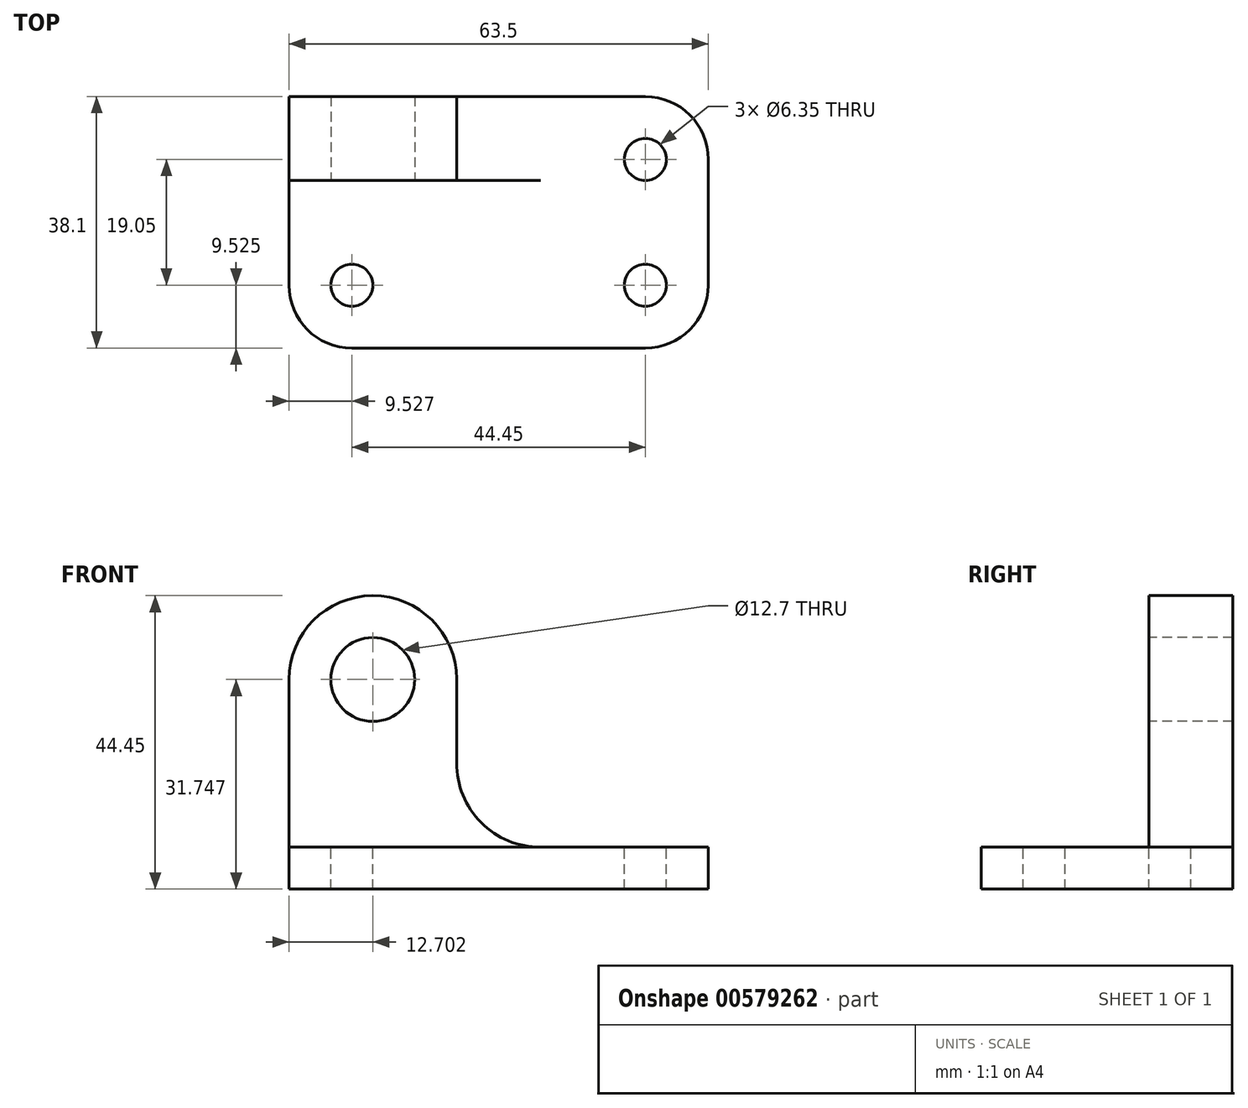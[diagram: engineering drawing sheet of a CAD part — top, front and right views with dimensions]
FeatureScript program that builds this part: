
annotation { "Feature Type Name" : "Feature", "Feature Type Description" : "" }
export const myFeature = defineFeature(function(context is Context, id is Id, definition is map)
    precondition{}
    {
        {
            var Q0;
            Q0=qCreatedBy(makeId("Front.planeOp"),FACE);
            var sketch = newSketch(context, id + "F0", { "sketchPlane" : qUnion([Q0])});
            skLineSegment(sketch, "E0", {"start": v(-165.52, 134.05) * mm, "end": v(-165.52, 89.6) * mm});
            skLineSegment(sketch, "E1", {"start": v(-165.52, 89.6) * mm, "end": v(-102.02, 89.6) * mm});
            skLineSegment(sketch, "E2", {"start": v(-102.02, 89.6) * mm, "end": v(-102.02, 95.95) * mm});
            skLineSegment(sketch, "E3", {"start": v(-102.02, 95.95) * mm, "end": v(-127.42, 95.95) * mm});
            skLineSegment(sketch, "E4", {"start": v(-127.42, 95.95) * mm, "end": v(-127.42, 134.05) * mm});
            skLineSegment(sketch, "E5", {"start": v(-127.42, 134.05) * mm, "end": v(-165.52, 134.05) * mm});
            skSolve(sketch);
        }
        {
            var Q0;
            Q0=makeQuery(id+"F0.imprint","IMPRINT",FACE,{"disambiguationData":[TD([[makeQuery(id+"F0.imprint","IMPRINT",EDGE,{"derivedFrom":sQuery(id+"F0.wireOp",EDGE,"E0")}),1.0]])]});
            extrude(context, id + "F1", {"entities" : qUnion([Q0]), "depth" : 38.1 * mm, "offsetDistance" : 25.4 * mm});
        }
        {
            var Q0;
            Q0=makeQuery(id+"F1.opExtrude","SWEPT_FACE",FACE,{"disambiguationData":[OSD([sQuery(id+"F0.wireOp",EDGE,"E4")])]});
            var sketch = newSketch(context, id + "F2", { "sketchPlane" : qUnion([Q0])});
            skLineSegment(sketch, "E6", {"start": v(-12.7, 134.05) * mm, "end": v(-12.7, 95.95) * mm});
            skSolve(sketch);
        }
        {
            var Q0;
            {var subQ0=sQuery(id+"F2.wireOp",EDGE,"E6");Q0=makeQuery(id+"F2.imprint","IMPRINT",FACE,{"disambiguationData":[TD([[makeQuery(id+"F2.imprint","IMPRINT",EDGE,{"derivedFrom":subQ0}),-1.0]])]});}
            extrude(context, id + "F3", {"entities" : qUnion([Q0]), "operationType" : NewBodyOperationType.REMOVE, "endBound" : BoundingType.THROUGH_ALL, "oppositeDirection" : true, "depth" : 25.4 * mm, "offsetDistance" : 25.4 * mm});
        }
        {
            var Q0;
            Q0=makeQuery(id+"F3.boolean.opBoolean","COPY",FACE,{"derivedFrom":makeQuery(id+"F3.opExtrude","SWEPT_FACE",FACE,{"disambiguationData":[OSD([sQuery(id+"F2.wireOp",EDGE,"E6")])]})});
            var sketch = newSketch(context, id + "F4", { "sketchPlane" : qUnion([Q0])});
            skCircle(sketch, "E7", {"center": v(-152.82, 121.35) * mm, "radius": 6.35 * mm});
            skCircle(sketch, "E8", {"center": v(-152.82, 121.35) * mm, "radius": 12.7 * mm});
            skSolve(sketch);
        }
        {
            var Q0;
            Q0=makeQuery(id+"F4.imprint","IMPRINT",FACE,{"disambiguationData":[TD([[makeQuery(id+"F4.imprint","IMPRINT",EDGE,{"derivedFrom":sQuery(id+"F4.wireOp",EDGE,"E7")}),1.0]])]});
            var Q1;
            {var subQ0=sQuery(id+"F4.wireOp",EDGE,"E8");var subQ1=sQuery(id+"F2.wireOp",EDGE,"E6");var subQ4=makeQuery(id+"F3.boolean.opBoolean","INTERSECT",EDGE,{"derivedFrom":[makeQuery(id+"F1.opExtrude","SWEPT_FACE",FACE,{"disambiguationData":[OSD([sQuery(id+"F0.wireOp",EDGE,"E0")])]}),makeQuery(id+"F3.opExtrude","SWEPT_FACE",FACE,{"disambiguationData":[OSD([subQ1])]})]});var subQ5=makeQuery(id+"F4.imprint","INTERSECT",VERTEX,{"derivedFrom":[subQ4,subQ0]});Q1=makeQuery(id+"F4.imprint","IMPRINT",FACE,{"disambiguationData":[TD([[makeQuery(id+"F4.imprint","IMPRINT",EDGE,{"disambiguationData":[TD([[subQ5,1.0]])],"derivedFrom":subQ0}),-1.0]])]});}
            extrude(context, id + "F5", {"entities" : qUnion([Q0, Q1]), "operationType" : NewBodyOperationType.REMOVE, "endBound" : BoundingType.THROUGH_ALL, "oppositeDirection" : true, "depth" : 25.4 * mm, "offsetDistance" : 25.4 * mm});
        }
        {
            var Q0;
            Q0=makeQuery(id+"F3.boolean.opBoolean","COPY",FACE,{"derivedFrom":makeQuery(id+"F3.opExtrude","SWEPT_FACE",FACE,{"disambiguationData":[OSD([sQuery(id+"F2.wireOp",EDGE,"E6")])]})});
            var sketch = newSketch(context, id + "F6", { "sketchPlane" : qUnion([Q0])});
            skArc(sketch, "E9", {"start": v(-140.12, 121.42) * mm, "mid": v(-143.86, 130.35) * mm, "end": v(-152.82, 134.05) * mm});
            skArc(sketch, "E10", {"start": v(-140.12, 108.72) * mm, "mid": v(-136.42, 99.7) * mm, "end": v(-127.42, 95.95) * mm});
            skPoint(sketch, "E10.startSnap0", {"position": v(-140.12, 134.05) * mm});
            skLineSegment(sketch, "E11", {"start": v(-140.12, 121.42) * mm, "end": v(-140.12, 108.72) * mm});
            skSolve(sketch);
        }
        {
            var Q0;
            Q0=makeQuery(id+"F6.imprint","IMPRINT",FACE,{"disambiguationData":[TD([[makeQuery(id+"F6.imprint","IMPRINT",EDGE,{"derivedFrom":sQuery(id+"F6.wireOp",EDGE,"E9")}),-1.0]])]});
            extrude(context, id + "F7", {"entities" : qUnion([Q0]), "operationType" : NewBodyOperationType.REMOVE, "endBound" : BoundingType.THROUGH_ALL, "oppositeDirection" : true, "depth" : 25.4 * mm, "offsetDistance" : 25.4 * mm});
        }
        {
            var Q0;
            {var subQ0=sQuery(id+"F0.wireOp",EDGE,"E3");Q0=makeQuery(id+"F3.boolean.opBoolean","MERGE",FACE,{"derivedFrom":[makeQuery(id+"F1.opExtrude","SWEPT_FACE",FACE,{"disambiguationData":[OSD([subQ0])]}),makeQuery(id+"F3.opExtrude","SWEPT_FACE",FACE,{"disambiguationData":[OSD([subQ0,sQuery(id+"F0.wireOp",EDGE,"E4")])]})]});}
            var sketch = newSketch(context, id + "F8", { "sketchPlane" : qUnion([Q0])});
            skCircle(sketch, "E12", {"center": v(-156, -28.58) * mm, "radius": 3.18 * mm});
            skCircle(sketch, "E13", {"center": v(-111.54, -28.58) * mm, "radius": 3.18 * mm});
            skCircle(sketch, "E14", {"center": v(-111.54, -9.52) * mm, "radius": 3.17 * mm});
            skSolve(sketch);
        }
        {
            var Q0;
            Q0=makeQuery(id+"F8.imprint","IMPRINT",FACE,{"disambiguationData":[TD([[makeQuery(id+"F8.imprint","IMPRINT",EDGE,{"derivedFrom":sQuery(id+"F8.wireOp",EDGE,"E12")}),1.0]])]});
            var Q1;
            Q1=makeQuery(id+"F8.imprint","IMPRINT",FACE,{"disambiguationData":[TD([[makeQuery(id+"F8.imprint","IMPRINT",EDGE,{"derivedFrom":sQuery(id+"F8.wireOp",EDGE,"E13")}),1.0]])]});
            var Q2;
            Q2=makeQuery(id+"F8.imprint","IMPRINT",FACE,{"disambiguationData":[TD([[makeQuery(id+"F8.imprint","IMPRINT",EDGE,{"derivedFrom":sQuery(id+"F8.wireOp",EDGE,"E14")}),1.0]])]});
            extrude(context, id + "F9", {"entities" : qUnion([Q0, Q1, Q2]), "operationType" : NewBodyOperationType.REMOVE, "endBound" : BoundingType.THROUGH_ALL, "oppositeDirection" : true, "depth" : 25.4 * mm, "offsetDistance" : 25.4 * mm});
        }
        {
            var Q0;
            {var subQ0=sQuery(id+"F0.wireOp",EDGE,"E3");Q0=makeQuery(id+"F3.boolean.opBoolean","MERGE",FACE,{"derivedFrom":[makeQuery(id+"F1.opExtrude","SWEPT_FACE",FACE,{"disambiguationData":[OSD([subQ0])]}),makeQuery(id+"F3.opExtrude","SWEPT_FACE",FACE,{"disambiguationData":[OSD([subQ0,sQuery(id+"F0.wireOp",EDGE,"E4")])]})]});}
            var sketch = newSketch(context, id + "F10", { "sketchPlane" : qUnion([Q0])});
            skCircle(sketch, "E15", {"center": v(-156, -28.58) * mm, "radius": 9.53 * mm});
            skCircle(sketch, "E16", {"center": v(-111.54, -28.58) * mm, "radius": 9.53 * mm});
            skCircle(sketch, "E17", {"center": v(-111.54, -9.52) * mm, "radius": 9.53 * mm});
            skSolve(sketch);
        }
        {
            var Q0;
            {var subQ0=sQuery(id+"F10.wireOp",EDGE,"E15");var subQ1=sQuery(id+"F0.wireOp",EDGE,"E4");var subQ2=sQuery(id+"F0.wireOp",EDGE,"E3");var subQ3=makeQuery(id+"F3.boolean.opBoolean","MERGE",EDGE,{"derivedFrom":[makeQuery(id+"F1.opExtrude","CAP_EDGE",EDGE,{"disambiguationData":[OSD([subQ2])],"isStart":false}),makeQuery(id+"F3.opExtrude","SWEPT_EDGE",EDGE,{"disambiguationData":[OSD([subQ2,subQ1])]})]});var subQ4=makeQuery(id+"F10.imprint","INTERSECT",VERTEX,{"derivedFrom":[subQ3,subQ0]});Q0=makeQuery(id+"F10.imprint","IMPRINT",FACE,{"disambiguationData":[TD([[makeQuery(id+"F10.imprint","IMPRINT",EDGE,{"disambiguationData":[TD([[subQ4,1.0]])],"derivedFrom":subQ0}),-1.0]])]});}
            var Q1;
            {var subQ0=sQuery(id+"F10.wireOp",EDGE,"E16");var subQ1=sQuery(id+"F0.wireOp",EDGE,"E3");var subQ2=makeQuery(id+"F1.opExtrude","SWEPT_EDGE",EDGE,{"disambiguationData":[OSD([sQuery(id+"F0.wireOp",EDGE,"E2"),subQ1])]});var subQ3=makeQuery(id+"F10.imprint","INTERSECT",VERTEX,{"derivedFrom":[subQ2,subQ0]});Q1=makeQuery(id+"F10.imprint","IMPRINT",FACE,{"disambiguationData":[TD([[makeQuery(id+"F10.imprint","IMPRINT",EDGE,{"disambiguationData":[TD([[subQ3,1.0]])],"derivedFrom":subQ0}),-1.0]])]});}
            var Q2;
            {var subQ0=sQuery(id+"F10.wireOp",EDGE,"E17");var subQ1=sQuery(id+"F0.wireOp",EDGE,"E3");var subQ2=makeQuery(id+"F1.opExtrude","CAP_EDGE",EDGE,{"disambiguationData":[OSD([subQ1])],"isStart":true});var subQ3=makeQuery(id+"F10.imprint","INTERSECT",VERTEX,{"derivedFrom":[subQ2,subQ0]});Q2=makeQuery(id+"F10.imprint","IMPRINT",FACE,{"disambiguationData":[TD([[makeQuery(id+"F10.imprint","IMPRINT",EDGE,{"disambiguationData":[TD([[subQ3,1.0]])],"derivedFrom":subQ0}),-1.0]])]});}
            extrude(context, id + "F11", {"entities" : qUnion([Q0, Q1, Q2]), "operationType" : NewBodyOperationType.REMOVE, "endBound" : BoundingType.THROUGH_ALL, "oppositeDirection" : true, "depth" : 25.4 * mm, "offsetDistance" : 25.4 * mm});
        }
    });
